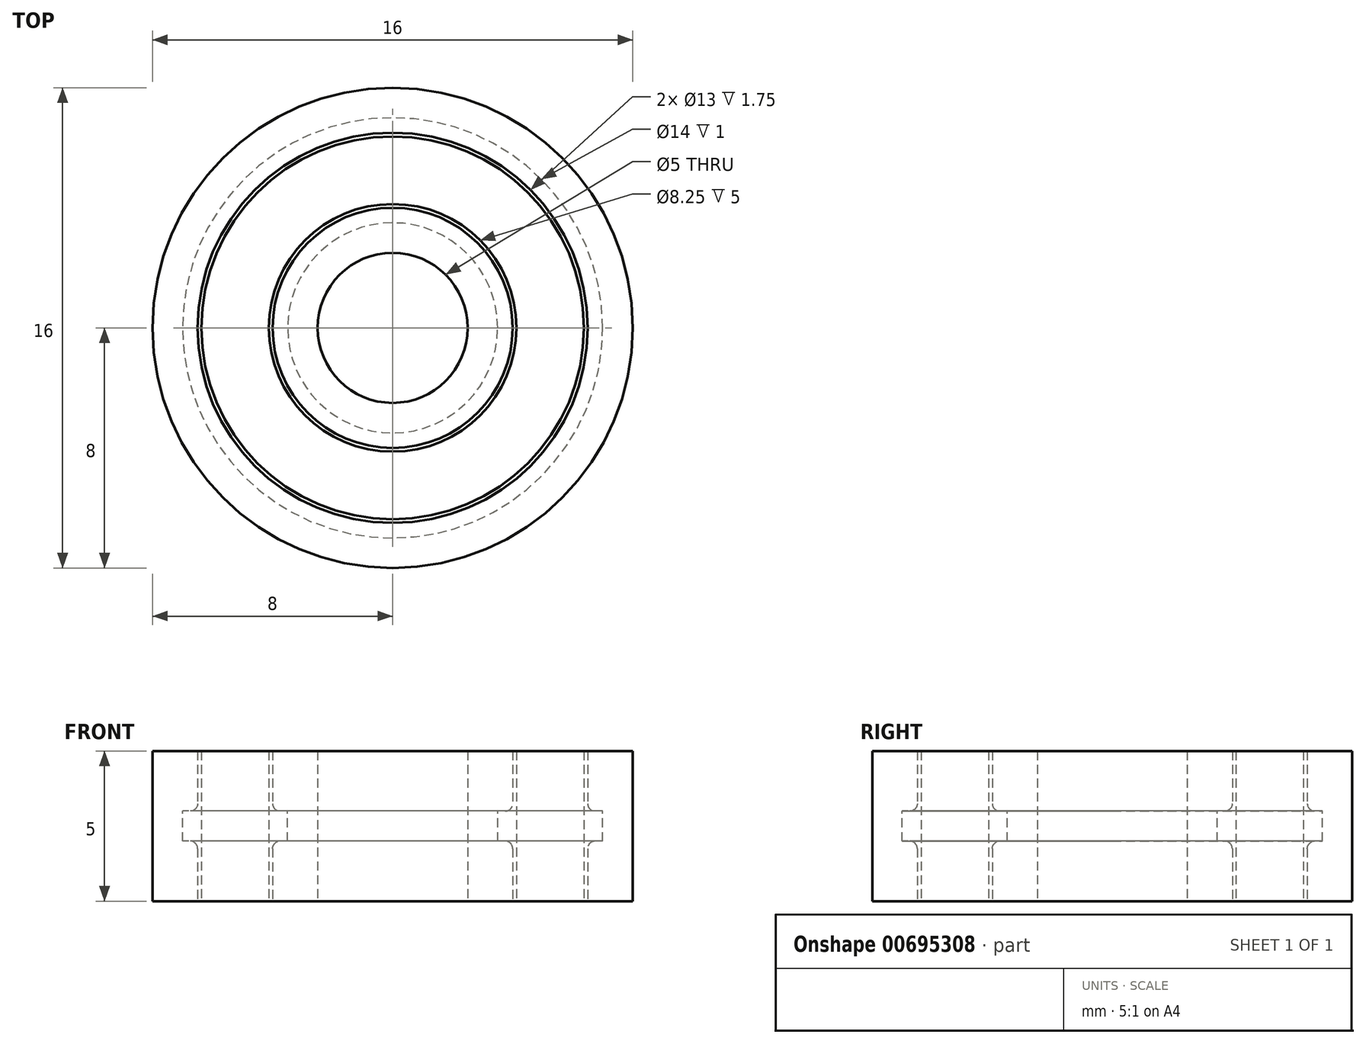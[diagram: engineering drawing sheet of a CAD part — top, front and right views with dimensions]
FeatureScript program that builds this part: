
annotation { "Feature Type Name" : "Feature", "Feature Type Description" : "" }
export const myFeature = defineFeature(function(context is Context, id is Id, definition is map)
    precondition{}
    {
        {
            var Q0;
            Q0=qCreatedBy(makeId("Top.planeOp"),FACE);
            var sketch = newSketch(context, id + "F0", { "sketchPlane" : qUnion([Q0])});
            skCircle(sketch, "E0", {"center": v(0, 0) * mm, "radius": 8 * mm});
            skCircle(sketch, "E1", {"center": v(0, 0) * mm, "radius": 2.5 * mm});
            skCircle(sketch, "E2", {"center": v(0, 0) * mm, "radius": 4 * mm});
            skCircle(sketch, "E3", {"center": v(0, 0) * mm, "radius": 6.5 * mm});
            skSolve(sketch);
        }
        {
            var Q0;
            Q0=makeQuery(id+"F0.imprint","IMPRINT",FACE,{"disambiguationData":[TD([[makeQuery(id+"F0.imprint","IMPRINT",EDGE,{"derivedFrom":sQuery(id+"F0.wireOp",EDGE,"E0")}),1.0]])]});
            var Q1;
            Q1=makeQuery(id+"F0.imprint","IMPRINT",FACE,{"disambiguationData":[TD([[makeQuery(id+"F0.imprint","IMPRINT",EDGE,{"derivedFrom":sQuery(id+"F0.wireOp",EDGE,"E1")}),-1.0]])]});
            extrude(context, id + "F1", {"entities" : qUnion([Q0, Q1]), "endBound" : BoundingType.SYMMETRIC, "depth" : 5 * mm, "offsetDistance" : 25.4 * mm});
        }
        {
            var Q0;
            Q0=qCreatedBy(makeId("Top.planeOp"),FACE);
            var sketch = newSketch(context, id + "F2", { "sketchPlane" : qUnion([Q0])});
            skCircle(sketch, "E4", {"center": v(0, 0) * mm, "radius": 3.5 * mm});
            skCircle(sketch, "E5", {"center": v(0, 0) * mm, "radius": 7 * mm});
            skSolve(sketch);
        }
        {
            var Q0;
            Q0=makeQuery(id+"F2.imprint","IMPRINT",FACE,{"disambiguationData":[TD([[makeQuery(id+"F2.imprint","IMPRINT",EDGE,{"derivedFrom":sQuery(id+"F2.wireOp",EDGE,"E4")}),-1.0]])]});
            extrude(context, id + "F3", {"entities" : qUnion([Q0]), "operationType" : NewBodyOperationType.REMOVE, "endBound" : BoundingType.SYMMETRIC, "oppositeDirection" : true, "depth" : 1 * mm, "offsetDistance" : 25.4 * mm});
        }
        {
            var Q0;
            Q0=makeQuery(id+"F3.boolean.opBoolean","INTERSECT",EDGE,{"derivedFrom":[makeQuery(id+"F1.opExtrude","SWEPT_FACE",FACE,{"disambiguationData":[OSD([sQuery(id+"F0.wireOp",EDGE,"E3")])]}),makeQuery(id+"F3.opExtrude","CAP_FACE",FACE,{"disambiguationData":[OSD([sQuery(id+"F2.wireOp",EDGE,"E4"),sQuery(id+"F2.wireOp",EDGE,"E5")])],"isStart":true})]});
            var Q1;
            Q1=makeQuery(id+"F3.boolean.opBoolean","INTERSECT",EDGE,{"derivedFrom":[makeQuery(id+"F1.opExtrude","SWEPT_FACE",FACE,{"disambiguationData":[OSD([sQuery(id+"F0.wireOp",EDGE,"E3")])]}),makeQuery(id+"F3.opExtrude","CAP_FACE",FACE,{"disambiguationData":[OSD([sQuery(id+"F2.wireOp",EDGE,"E4"),sQuery(id+"F2.wireOp",EDGE,"E5")])],"isStart":false})]});
            var Q2;
            Q2=makeQuery(id+"F3.boolean.opBoolean","INTERSECT",EDGE,{"derivedFrom":[makeQuery(id+"F1.opExtrude","SWEPT_FACE",FACE,{"disambiguationData":[OSD([sQuery(id+"F0.wireOp",EDGE,"E2")])]}),makeQuery(id+"F3.opExtrude","CAP_FACE",FACE,{"disambiguationData":[OSD([sQuery(id+"F2.wireOp",EDGE,"E4"),sQuery(id+"F2.wireOp",EDGE,"E5")])],"isStart":false})]});
            var Q3;
            Q3=makeQuery(id+"F3.boolean.opBoolean","INTERSECT",EDGE,{"derivedFrom":[makeQuery(id+"F1.opExtrude","SWEPT_FACE",FACE,{"disambiguationData":[OSD([sQuery(id+"F0.wireOp",EDGE,"E2")])]}),makeQuery(id+"F3.opExtrude","CAP_FACE",FACE,{"disambiguationData":[OSD([sQuery(id+"F2.wireOp",EDGE,"E4"),sQuery(id+"F2.wireOp",EDGE,"E5")])],"isStart":true})]});
            fillet(context, id + "F4", {"entities" : qUnion([Q0, Q1, Q2, Q3]), "radius" : .25 * mm, "tangentPropagation" : true, "allowEdgeOverflow" : false});
        }
        {
            var Q0;
            Q0=makeQuery(id+"F1.opExtrude","CAP_FACE",FACE,{"disambiguationData":[OSD([sQuery(id+"F0.wireOp",EDGE,"E0"),sQuery(id+"F0.wireOp",EDGE,"E3")])],"isStart":true});
            var sketch = newSketch(context, id + "F5", { "sketchPlane" : qUnion([Q0])});
            skCircle(sketch, "E6", {"center": v(0, 0) * mm, "radius": 6.38 * mm});
            skCircle(sketch, "E7", {"center": v(0, 0) * mm, "radius": 4.12 * mm});
            skSolve(sketch);
        }
        {
            var Q0;
            Q0=makeQuery(id+"F5.imprint","IMPRINT",FACE,{"disambiguationData":[TD([[makeQuery(id+"F5.imprint","IMPRINT",EDGE,{"derivedFrom":sQuery(id+"F5.wireOp",EDGE,"E6")}),1.0]])]});
            extrude(context, id + "F6", {"entities" : qUnion([Q0]), "oppositeDirection" : true, "depth" : 5 * mm, "offsetDistance" : 25.4 * mm});
        }
    });
